# Revit family: xShower_Arm-American_Standard-Standard-1660.240
name_source: partatom
category: Plumbing Fixtures
revit_build: Autodesk Revit 2014 (Build: 20130308_1515(x64)
units: mm (PartAtom-declared; Revit-internal decimal feet)

## types (1)
- 1660.240
    Assembly Code = D2010700
    CW Connection = Yes
    CWFU = 3
    Default Elevation = 78"
    Description = Standard Shower Arm
    Finish = Brass-American Standard-002-Polished Chrome
    HW Connection = Yes
    HWFU = 3
    Installation Type = Wall Mounted
    Length = 5 1/2"
    Manufacturer = American Standard
    Material = Brass-American Standard-002-Polished Chrome
    Model = 1660.240
    Price = Prices may vary. Please consult Manufacturer Representative for most up-to-date price list.
    Product Documentation Link = https://www.americanstandard-us.com
    Product Page URL = https://www.americanstandard-us.com
    URL = https://www.americanstandard-us.com
    Vent Connection = No
    WFU = 4
    Warranty Information = One Year Limited Warranty
    Waste Connection = No
    Water Connection Diameter = 1/2"
    Water Connection Radius = 1/4"
    Width = 2"

## geometry (parser evidence)
native form markers: Sweep x3
no freeform markers — native parametric forms only
